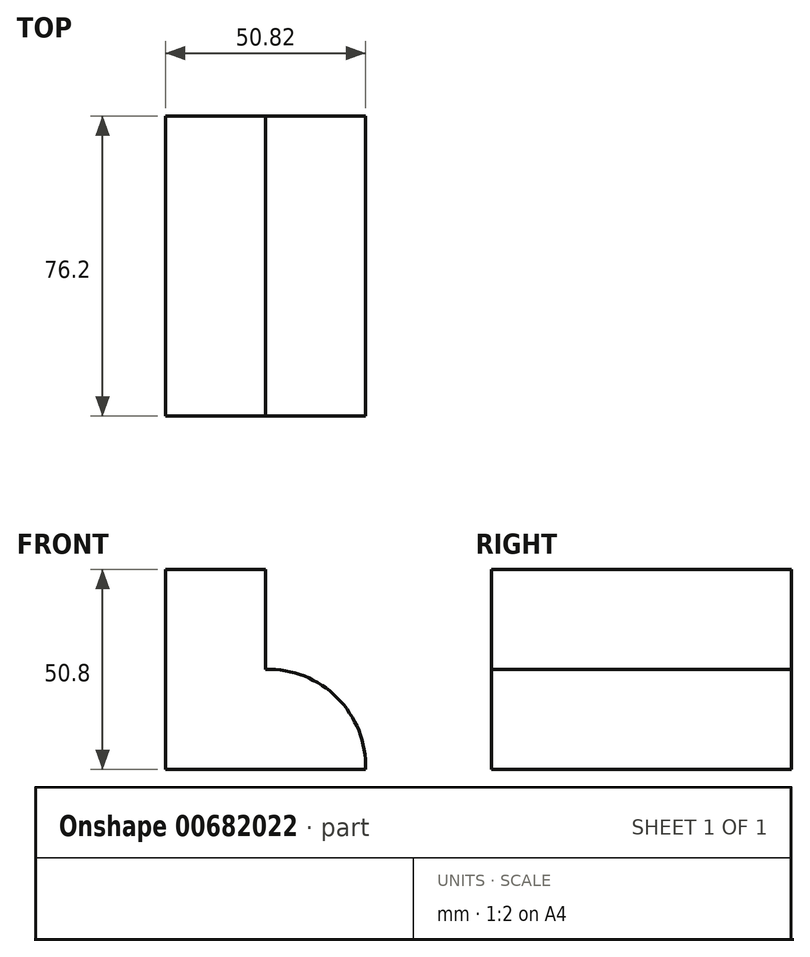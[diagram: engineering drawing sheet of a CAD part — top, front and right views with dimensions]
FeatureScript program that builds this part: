
annotation { "Feature Type Name" : "Feature", "Feature Type Description" : "" }
export const myFeature = defineFeature(function(context is Context, id is Id, definition is map)
    precondition{}
    {
        {
            var Q0;
            Q0=qCreatedBy(makeId("Front.planeOp"),FACE);
            var sketch = newSketch(context, id + "F0", { "sketchPlane" : qUnion([Q0])});
            skLineSegment(sketch, "E0", {"start": v(-1.7, 7.89) * mm, "end": v(-52.5, 7.89) * mm});
            skLineSegment(sketch, "E1", {"start": v(-52.5, 7.89) * mm, "end": v(-52.5, 58.69) * mm});
            skLineSegment(sketch, "E2", {"start": v(-52.5, 58.69) * mm, "end": v(-27.1, 58.69) * mm});
            skLineSegment(sketch, "E3", {"start": v(-27.1, 58.69) * mm, "end": v(-27.1, 33.29) * mm});
            skArc(sketch, "E4", {"start": v(-1.7, 7.89) * mm, "mid": v(-8.88, 26.1) * mm, "end": v(-27.1, 33.29) * mm});
            skSolve(sketch);
        }
        {
            var Q0;
            Q0 = qSketchRegion(id + "F0", true);
            extrude(context, id + "F1", {"entities" : qUnion([Q0]), "depth" : 76.2 * mm, "offsetDistance" : 25.4 * mm});
        }
    });
